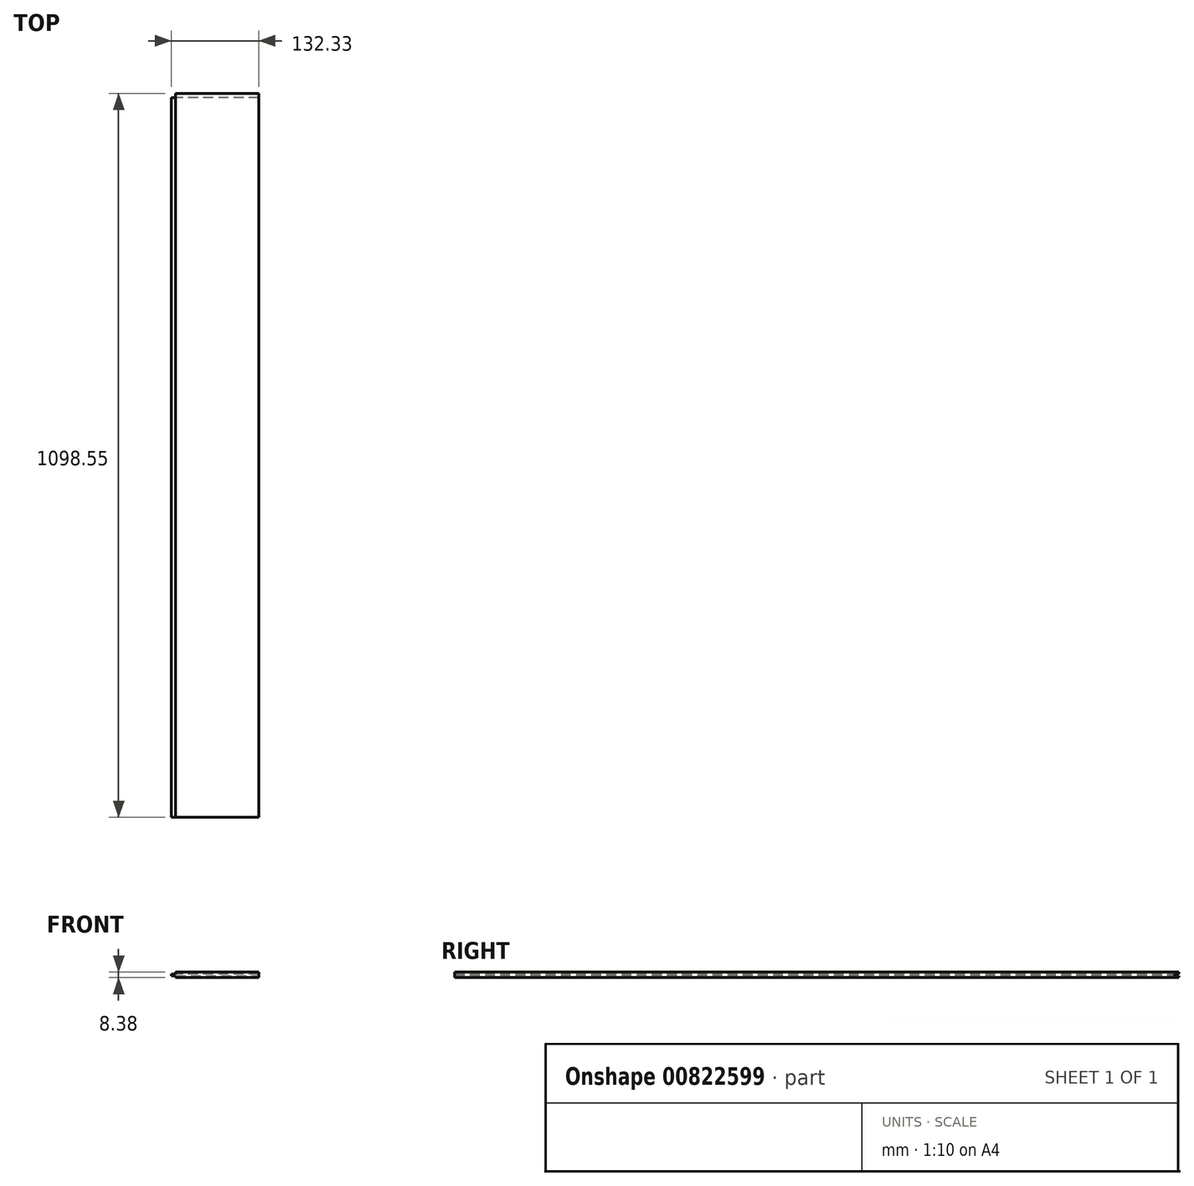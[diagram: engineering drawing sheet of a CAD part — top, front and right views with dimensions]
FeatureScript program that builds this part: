
annotation { "Feature Type Name" : "Feature", "Feature Type Description" : "" }
export const myFeature = defineFeature(function(context is Context, id is Id, definition is map)
    precondition{}
    {
        {
            var Q0;
            Q0=qCreatedBy(makeId("Front.planeOp"),FACE);
            var sketch = newSketch(context, id + "F0", { "sketchPlane" : qUnion([Q0])});
            skLineSegment(sketch, "E0.bottom", {"start": v(0, 0) * mm, "end": v(125.98, 0) * mm});
            skLineSegment(sketch, "E0.top", {"start": v(0, -8.38) * mm, "end": v(125.98, -8.38) * mm});
            skLineSegment(sketch, "E0.left", {"start": v(0, 0) * mm, "end": v(0, -8.38) * mm});
            skLineSegment(sketch, "E0.right", {"start": v(125.98, 0) * mm, "end": v(125.98, -8.38) * mm});
            skSolve(sketch);
        }
        {
            var Q0;
            Q0=qSketchRegion(id+"F0",true);
            extrude(context, id + "F1", {"entities" : qUnion([Q0]), "depth" : 1290.07 * mm, "offsetDistance" : 25.4 * mm});
        }
        {
            var Q0;
            Q0=makeQuery(id+"F0.imprint","IMPRINT",FACE,{"disambiguationData":[TD([[makeQuery(id+"F0.imprint","IMPRINT",EDGE,{"derivedFrom":sQuery(id+"F0.wireOp",EDGE,"E0.bottom")}),-1.0]])]});
            var sketch = newSketch(context, id + "F2", { "sketchPlane" : qUnion([Q0])});
            skLineSegment(sketch, "E1.bottom", {"start": v(0, -2.8) * mm, "end": v(-6.35, -2.8) * mm});
            skLineSegment(sketch, "E1.top", {"start": v(0, -5.59) * mm, "end": v(-6.35, -5.59) * mm});
            skLineSegment(sketch, "E1.left", {"start": v(0, -2.8) * mm, "end": v(0, -5.59) * mm});
            skLineSegment(sketch, "E1.right", {"start": v(-6.35, -2.8) * mm, "end": v(-6.35, -5.59) * mm});
            skSolve(sketch);
        }
        {
            var Q0;
            Q0=makeQuery(id+"F2.imprint","IMPRINT",FACE,{"disambiguationData":[TD([[makeQuery(id+"F2.imprint","IMPRINT",EDGE,{"derivedFrom":sQuery(id+"F2.wireOp",EDGE,"E1.bottom")}),1.0]])]});
            extrude(context, id + "F3", {"entities" : qUnion([Q0]), "operationType" : NewBodyOperationType.ADD, "endBound" : BoundingType.THROUGH_ALL, "depth" : 25.4 * mm, "offsetDistance" : 25.4 * mm});
        }
        {
            var Q0;
            Q0=makeQuery(id+"F3.opExtrude","SWEPT_FACE",FACE,{"disambiguationData":[OSD([sQuery(id+"F2.wireOp",EDGE,"E1.right")])]});
            var sketch = newSketch(context, id + "F4", { "sketchPlane" : qUnion([Q0])});
            skLineSegment(sketch, "E2.bottom", {"start": v(1296.87, -2.8) * mm, "end": v(1296.42, -2.8) * mm});
            skLineSegment(sketch, "E2.top", {"start": v(1296.87, -5.59) * mm, "end": v(1296.42, -5.59) * mm});
            skLineSegment(sketch, "E2.left", {"start": v(1296.87, -2.8) * mm, "end": v(1296.87, -5.59) * mm});
            skLineSegment(sketch, "E2.right", {"start": v(1296.42, -2.8) * mm, "end": v(1296.42, -5.59) * mm});
            skSolve(sketch);
        }
        {
            var Q0;
            Q0=qSketchRegion(id+"F4",true);
            extrude(context, id + "F5", {"entities" : qUnion([Q0]), "operationType" : NewBodyOperationType.REMOVE, "endBound" : BoundingType.THROUGH_ALL, "oppositeDirection" : true, "depth" : 25.4 * mm, "offsetDistance" : 25.4 * mm});
        }
        {
            var Q0;
            Q0=makeQuery(id+"F3.opExtrude","SWEPT_FACE",FACE,{"disambiguationData":[OSD([sQuery(id+"F2.wireOp",EDGE,"E1.right")])]});
            var sketch = newSketch(context, id + "F6", { "sketchPlane" : qUnion([Q0])});
            skLineSegment(sketch, "E3.bottom", {"start": v(1296.42, -2.8) * mm, "end": v(1290.07, -2.8) * mm});
            skLineSegment(sketch, "E3.top", {"start": v(1296.42, -5.59) * mm, "end": v(1290.07, -5.59) * mm});
            skLineSegment(sketch, "E3.left", {"start": v(1296.42, -2.8) * mm, "end": v(1296.42, -5.59) * mm});
            skLineSegment(sketch, "E3.right", {"start": v(1290.07, -2.8) * mm, "end": v(1290.07, -5.59) * mm});
            skSolve(sketch);
        }
        {
            var Q0;
            Q0=qSketchRegion(id+"F6",true);
            var Q1;
            Q1=makeQuery(id+"F1.opExtrude","SWEPT_FACE",FACE,{"disambiguationData":[OSD([sQuery(id+"F0.wireOp",EDGE,"E0.right")])]});
            extrude(context, id + "F7", {"entities" : qUnion([Q0]), "operationType" : NewBodyOperationType.ADD, "endBound" : BoundingType.UP_TO_SURFACE, "oppositeDirection" : true, "depth" : 25.4 * mm, "endBoundEntityFace" : qUnion([Q1]), "offsetDistance" : 25.4 * mm});
        }
        {
            var Q0;
            Q0=makeQuery(id+"F3.boolean.opBoolean","MERGE",FACE,{"derivedFrom":[makeQuery(id+"F1.opExtrude","CAP_FACE",FACE,{"disambiguationData":[OSD([sQuery(id+"F0.wireOp",EDGE,"E0.bottom"),sQuery(id+"F0.wireOp",EDGE,"E0.top"),sQuery(id+"F0.wireOp",EDGE,"E0.left"),sQuery(id+"F0.wireOp",EDGE,"E0.right")])],"isStart":true}),makeQuery(id+"F3.opExtrude","CAP_FACE",FACE,{"disambiguationData":[OSD([sQuery(id+"F2.wireOp",EDGE,"E1.bottom"),sQuery(id+"F2.wireOp",EDGE,"E1.top"),sQuery(id+"F2.wireOp",EDGE,"E1.left"),sQuery(id+"F2.wireOp",EDGE,"E1.right")])],"isStart":true})]});
            var sketch = newSketch(context, id + "F8", { "sketchPlane" : qUnion([Q0])});
            skLineSegment(sketch, "E4.bottom", {"start": v(6.35, -2.8) * mm, "end": v(-125.98, -2.8) * mm});
            skLineSegment(sketch, "E4.top", {"start": v(6.35, -5.59) * mm, "end": v(-125.98, -5.59) * mm});
            skLineSegment(sketch, "E4.left", {"start": v(6.35, -2.8) * mm, "end": v(6.35, -5.59) * mm});
            skLineSegment(sketch, "E4.right", {"start": v(-125.98, -2.8) * mm, "end": v(-125.98, -5.59) * mm});
            skSolve(sketch);
        }
        {
            var Q0;
            {var subQ0=sQuery(id+"F8.wireOp",EDGE,"E4.left");Q0=makeQuery(id+"F8.imprint","IMPRINT",FACE,{"disambiguationData":[TD([[makeQuery(id+"F8.imprint","IMPRINT",EDGE,{"derivedFrom":subQ0}),-1.0]])]});}
            extrude(context, id + "F9", {"entities" : qUnion([Q0]), "operationType" : NewBodyOperationType.REMOVE, "oppositeDirection" : true, "depth" : 6.35 * mm, "offsetDistance" : 25.4 * mm});
        }
        {
            var Q0;
            Q0=makeQuery(id+"F7.boolean.opBoolean","MERGE",FACE,{"derivedFrom":[makeQuery(id+"F3.opExtrude","SWEPT_FACE",FACE,{"disambiguationData":[OSD([sQuery(id+"F2.wireOp",EDGE,"E1.bottom")])]}),makeQuery(id+"F7.opExtrude","SWEPT_FACE",FACE,{"disambiguationData":[OSD([sQuery(id+"F6.wireOp",EDGE,"E3.bottom")])]})]});
            var sketch = newSketch(context, id + "F10", { "sketchPlane" : qUnion([Q0])});
            skLineSegment(sketch, "E5.bottom", {"start": v(125.98, -1296.42) * mm, "end": v(-1418.6, -1296.42) * mm});
            skLineSegment(sketch, "E5.top", {"start": v(125.98, -1098.55) * mm, "end": v(-1418.6, -1098.55) * mm});
            skLineSegment(sketch, "E5.left", {"start": v(125.98, -1296.42) * mm, "end": v(125.98, -1098.55) * mm});
            skLineSegment(sketch, "E5.right", {"start": v(-1418.6, -1296.42) * mm, "end": v(-1418.6, -1098.55) * mm});
            skSolve(sketch);
        }
        {
            var Q0;
            Q0 = qSketchRegion(id + "F10", true);
            extrude(context, id + "F11", {"entities" : qUnion([Q0]), "operationType" : NewBodyOperationType.REMOVE, "depth" : 25.4 * mm, "offsetDistance" : 25.4 * mm, "hasSecondDirection" : true, "secondDirectionOppositeDirection" : true, "secondDirectionDepth" : 25.4 * mm});
        }
        {
            var Q0;
            Q0=makeQuery(id+"F1.opExtrude","SWEPT_BODY",BODY,{"disambiguationData":[OSD([sQuery(id+"F0.wireOp",EDGE,"E0.bottom"),sQuery(id+"F0.wireOp",EDGE,"E0.top"),sQuery(id+"F0.wireOp",EDGE,"E0.left"),sQuery(id+"F0.wireOp",EDGE,"E0.right")])]});
            transform(context, id + "F12", {"entities" : qUnion([Q0]), "transformType" : TransformType.TRANSLATION_3D, "dx" : 0 * mm, "dy" : 0 * mm, "dz" : 0 * mm, "makeCopy" : true});
        }
    });
